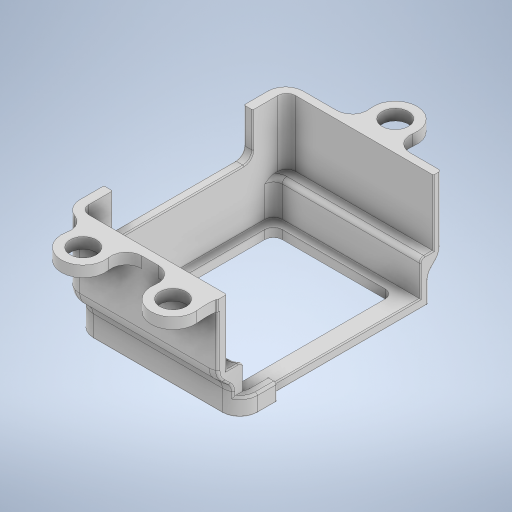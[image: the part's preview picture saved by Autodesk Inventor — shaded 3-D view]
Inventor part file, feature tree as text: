
AUTODESK INVENTOR PART (.ipt)
format: ipt  version: 2024 (Build 280153000, 153)  size: 1,560,576 bytes
history: native  units: in
note: dims shown in document units (in); Inventor stores cm internally (conversion verified against a paired STEP export)
features: extrude x8, fillet x8, chamfer x2, projected_geometry x2, plane x1
ambient origin geometry x8: Origin, YZ Plane, XZ Plane, XY Plane, X Axis, Y Axis, Z Axis, Center Point
bodies: Body1 (feature_tree)
feature tree (21):
  extrude  "Extrusion3"  Depth=0.0787in
  plane  "Work Plane1"
  extrude  "Extrusion4"  Depth=0.0787in
  extrude  "Extrusion7"  Depth=0.0787in TaperAngle=0.0deg
  extrude  "Extrusion8"  Depth=0.315in TaperAngle=0.0deg
  extrude  "Extrusion10"  Depth=0.315in
  extrude  "Extrusion11"  Depth=0.0787in TaperAngle=0.0deg
  extrude  "Extrusion12"  Depth=0.5906in TaperAngle=0.0deg
  extrude  "Extrusion13"  Depth=0.3937in
  chamfer  "Chamfer1"  Distance=0.2362in
  fillet  "Fillet1"  Radius=0.3937in
  fillet  "Fillet2"  Radius=0.2362in
  chamfer  "Chamfer2"  Distance=0.3937in
  fillet  "Fillet3"  Radius=0.8071in
  fillet  "Fillet4"  Radius=0.0984in
  fillet  "Fillet5"  Radius=0.1575in
  fillet  "Fillet6"  Radius=1.4646in
  fillet  "Fillet7"  Radius=1.0827in
  fillet  "Fillet8"  Radius=0.1575in
  projected_geometry  "Projected Loop3"
  projected_geometry  "Projected Loop4"
